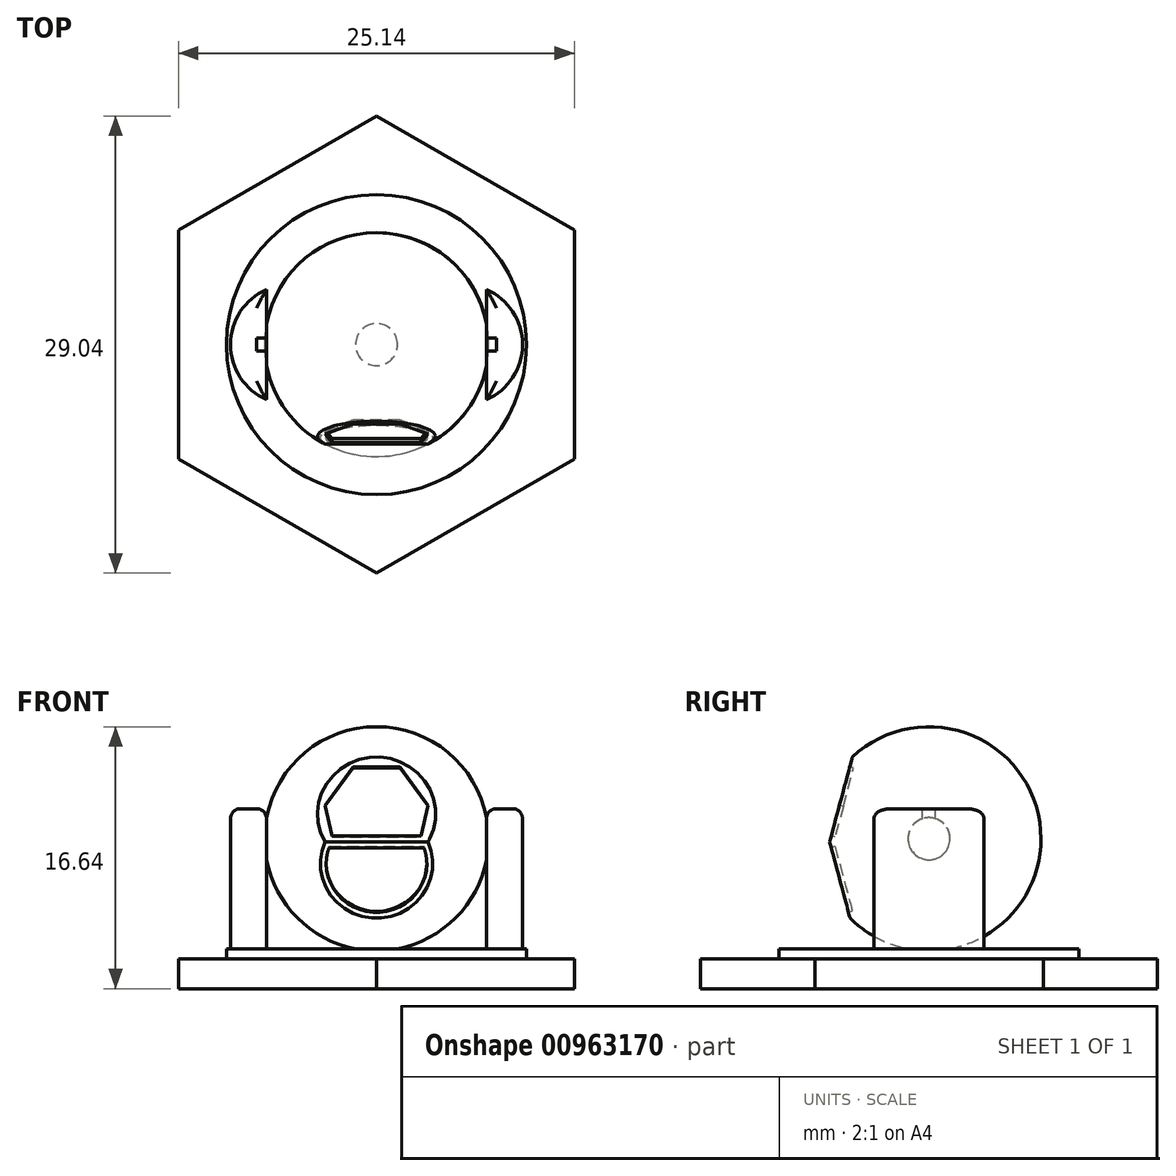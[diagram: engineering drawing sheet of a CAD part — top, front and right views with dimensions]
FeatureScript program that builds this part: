
annotation { "Feature Type Name" : "Feature", "Feature Type Description" : "" }
export const myFeature = defineFeature(function(context is Context, id is Id, definition is map)
    precondition{}
    {
        {
            var Q0;
            Q0=qCreatedBy(makeId("Top.planeOp"),FACE);
            var sketch = newSketch(context, id + "F0", { "sketchPlane" : qUnion([Q0])});
            skCircle(sketch, "E0.cCircle", {"center": v(0, 0) * mm, "radius": 12.57 * mm, "construction": true});
            skLineSegment(sketch, "E0.0", {"start": v(0, 14.52) * mm, "end": v(12.57, 7.26) * mm});
            skLineSegment(sketch, "E0.1", {"start": v(12.57, 7.26) * mm, "end": v(12.57, -7.26) * mm});
            skLineSegment(sketch, "E0.2", {"start": v(12.57, -7.26) * mm, "end": v(0, -14.52) * mm});
            skLineSegment(sketch, "E0.3", {"start": v(0, -14.52) * mm, "end": v(-12.57, -7.26) * mm});
            skLineSegment(sketch, "E0.4", {"start": v(-12.57, -7.26) * mm, "end": v(-12.57, 7.26) * mm});
            skLineSegment(sketch, "E0.5", {"start": v(-12.57, 7.26) * mm, "end": v(0, 14.52) * mm});
            skPoint(sketch, "E0.0.midPoint", {"position": v(6.29, 10.89) * mm});
            skLineSegment(sketch, "E1", {"start": v(-6.99, 3.5) * mm, "end": v(-6.99, -3.5) * mm});
            skArc(sketch, "E2", {"start": v(-6.99, 3.5) * mm, "mid": v(-9.27, 0) * mm, "end": v(-6.99, -3.5) * mm});
            skLineSegment(sketch, "E3.MirrorCS", {"start": v(6.99, 3.5) * mm, "end": v(6.99, -3.5) * mm});
            skArc(sketch, "E4.MirrorCS", {"start": v(6.99, 3.5) * mm, "mid": v(9.27, 0) * mm, "end": v(6.99, -3.5) * mm});
            skCircle(sketch, "E5", {"center": v(0, 0) * mm, "radius": 9.53 * mm});
            skSolve(sketch);
        }
        {
            var Q0;
            Q0=makeQuery(id+"F0.imprint","IMPRINT",FACE,{"disambiguationData":[TD([[makeQuery(id+"F0.imprint","IMPRINT",EDGE,{"derivedFrom":sQuery(id+"F0.wireOp",EDGE,"E0.0")}),-1.0]])]});
            var Q1;
            Q1=makeQuery(id+"F0.imprint","IMPRINT",FACE,{"disambiguationData":[TD([[makeQuery(id+"F0.imprint","IMPRINT",EDGE,{"derivedFrom":sQuery(id+"F0.wireOp",EDGE,"E1")}),1.0]])]});
            extrude(context, id + "F1", {"entities" : qUnion([Q0, Q1]), "depth" : 1.9 * mm, "offsetDistance" : 25.4 * mm});
        }
        {
            var Q0;
            Q0=makeQuery(id+"F0.imprint","IMPRINT",FACE,{"disambiguationData":[TD([[makeQuery(id+"F0.imprint","IMPRINT",EDGE,{"derivedFrom":sQuery(id+"F0.wireOp",EDGE,"E1")}),-1.0]])]});
            var Q1;
            Q1=makeQuery(id+"F0.imprint","IMPRINT",FACE,{"disambiguationData":[TD([[makeQuery(id+"F0.imprint","IMPRINT",EDGE,{"derivedFrom":sQuery(id+"F0.wireOp",EDGE,"E3.MirrorCS")}),1.0]])]});
            extrude(context, id + "F2", {"entities" : qUnion([Q0, Q1]), "operationType" : NewBodyOperationType.ADD, "depth" : 11.43 * mm, "offsetDistance" : 25.4 * mm});
        }
        {
            var Q0;
            Q0=makeQuery(id+"F1.opExtrude","CAP_FACE",FACE,{"disambiguationData":[OSD([sQuery(id+"F0.wireOp",EDGE,"E0.0"),sQuery(id+"F0.wireOp",EDGE,"E0.1"),sQuery(id+"F0.wireOp",EDGE,"E0.2"),sQuery(id+"F0.wireOp",EDGE,"E0.3"),sQuery(id+"F0.wireOp",EDGE,"E0.4"),sQuery(id+"F0.wireOp",EDGE,"E0.5"),sQuery(id+"F0.wireOp",EDGE,"E1"),sQuery(id+"F0.wireOp",EDGE,"E2"),sQuery(id+"F0.wireOp",EDGE,"E3.MirrorCS"),sQuery(id+"F0.wireOp",EDGE,"E4.MirrorCS")])],"isStart":false});
            cPlane(context, id + "F3", {"entities" : qUnion([Q0]), "cplaneType" : CPlaneType.OFFSET, "offset" : 7.62 * mm, "width" : 152.4 * mm, "height" : 152.4 * mm});
        }
        {
            var Q0;
            Q0=qCreatedBy(id+"F3.planeOp",FACE);
            var sketch = newSketch(context, id + "F4", { "sketchPlane" : qUnion([Q0])});
            skLineSegment(sketch, "E6", {"start": v(0, -7.11) * mm, "end": v(0, 7.11) * mm});
            skArc(sketch, "E7", {"start": v(0, 7.11) * mm, "mid": v(-7.11, 0) * mm, "end": v(0, -7.11) * mm});
            skLineSegment(sketch, "E8", {"start": v(-7.11, 0) * mm, "end": v(0, 0) * mm, "construction": true});
            skSolve(sketch);
        }
        {
            var Q0;
            Q0=makeQuery(id+"F4.imprint","IMPRINT",FACE,{"disambiguationData":[TD([[makeQuery(id+"F4.imprint","IMPRINT",EDGE,{"derivedFrom":sQuery(id+"F4.wireOp",EDGE,"E6")}),1.0]])]});
            var Q1;
            Q1=sQuery(id+"F4.wireOp",EDGE,"E6");
            revolve(context, id + "F5", {"operationType" : NewBodyOperationType.ADD, "surfaceOperationType" : NewSurfaceOperationType.NEW, "entities" : qUnion([Q0]), "axis" : qUnion([Q1]), "revolveType" : RevolveType.FULL});
        }
        {
            var Q0;
            Q0=makeQuery(id+"F2.opExtrude","CAP_FACE",FACE,{"disambiguationData":[OSD([sQuery(id+"F0.wireOp",EDGE,"E1"),sQuery(id+"F0.wireOp",EDGE,"E2")])],"isStart":false});
            var Q1;
            Q1=makeQuery(id+"F2.opExtrude","CAP_FACE",FACE,{"disambiguationData":[OSD([sQuery(id+"F0.wireOp",EDGE,"E3.MirrorCS"),sQuery(id+"F0.wireOp",EDGE,"E4.MirrorCS")])],"isStart":false});
            fillet(context, id + "F6", {"entities" : qUnion([Q0, Q1]), "radius" : 0.64 * mm, "tangentPropagation" : true, "allowEdgeOverflow" : false});
        }
        {
            var Q0;
            Q0=makeQuery(id+"F0.imprint","IMPRINT",FACE,{"disambiguationData":[TD([[makeQuery(id+"F0.imprint","IMPRINT",EDGE,{"derivedFrom":sQuery(id+"F0.wireOp",EDGE,"E1")}),1.0]])]});
            extrude(context, id + "F7", {"entities" : qUnion([Q0]), "operationType" : NewBodyOperationType.ADD, "depth" : 2.54 * mm, "offsetDistance" : 25.4 * mm});
        }
        {
            var Q0;
            Q0=sQuery(id+"F4.wireOp",EDGE,"E8");
            cPlane(context, id + "F8", {"entities" : qUnion([Q0]), "cplaneType" : CPlaneType.LINE_ANGLE, "offset" : 25.4 * mm, "angle" : 105 * degree, "width" : 152.4 * mm, "height" : 152.4 * mm});
        }
        {
            var Q0;
            Q0=sQuery(id+"F4.wireOp",EDGE,"E8");
            cPlane(context, id + "F9", {"entities" : qUnion([Q0]), "cplaneType" : CPlaneType.LINE_ANGLE, "offset" : 25.4 * mm, "angle" : 105 * degree, "oppositeDirection" : true, "width" : 152.4 * mm, "height" : 152.4 * mm});
        }
        {
            var Q0;
            Q0=qCreatedBy(id+"F8.planeOp",FACE);
            var sketch = newSketch(context, id + "F10", { "sketchPlane" : qUnion([Q0])});
            skLineSegment(sketch, "E9.bottom", {"start": v(-5.08, -3.68) * mm, "end": v(5.08, -3.68) * mm});
            skLineSegment(sketch, "E9.top", {"start": v(-5.08, -4.95) * mm, "end": v(5.08, -4.95) * mm});
            skLineSegment(sketch, "E9.left", {"start": v(-5.08, -3.68) * mm, "end": v(-5.08, -4.95) * mm});
            skLineSegment(sketch, "E9.right", {"start": v(5.08, -3.68) * mm, "end": v(5.08, -4.95) * mm});
            skSolve(sketch);
        }
        {
            var Q0;
            Q0=makeQuery(id+"F10.imprint","IMPRINT",FACE,{"disambiguationData":[TD([[makeQuery(id+"F10.imprint","IMPRINT",EDGE,{"derivedFrom":sQuery(id+"F10.wireOp",EDGE,"E9.bottom")}),-1.0]])]});
            extrude(context, id + "F11", {"entities" : qUnion([Q0]), "operationType" : NewBodyOperationType.REMOVE, "oppositeDirection" : true, "depth" : 7.62 * mm, "offsetDistance" : 25.4 * mm, "symmetric" : true});
        }
        {
            var Q0;
            Q0=qCreatedBy(id+"F9.planeOp",FACE);
            var sketch = newSketch(context, id + "F12", { "sketchPlane" : qUnion([Q0])});
            skLineSegment(sketch, "E10.bottom", {"start": v(-5.08, 8.5) * mm, "end": v(5.08, 8.5) * mm});
            skLineSegment(sketch, "E10.top", {"start": v(-5.08, 10.41) * mm, "end": v(5.08, 10.41) * mm});
            skLineSegment(sketch, "E10.left", {"start": v(-5.08, 8.5) * mm, "end": v(-5.08, 10.41) * mm});
            skLineSegment(sketch, "E10.right", {"start": v(5.08, 8.5) * mm, "end": v(5.08, 10.41) * mm});
            skSolve(sketch);
        }
        {
            var Q0;
            Q0=makeQuery(id+"F12.imprint","IMPRINT",FACE,{"disambiguationData":[TD([[makeQuery(id+"F12.imprint","IMPRINT",EDGE,{"derivedFrom":sQuery(id+"F12.wireOp",EDGE,"E10.bottom")}),1.0]])]});
            extrude(context, id + "F13", {"entities" : qUnion([Q0]), "operationType" : NewBodyOperationType.REMOVE, "oppositeDirection" : true, "depth" : 7.62 * mm, "offsetDistance" : 25.4 * mm, "symmetric" : true});
        }
        {
            var Q0;
            Q0=makeQuery(id+"F11.boolean.opBoolean","COPY",FACE,{"derivedFrom":makeQuery(id+"F11.opExtrude","SWEPT_FACE",FACE,{"disambiguationData":[OSD([sQuery(id+"F10.wireOp",EDGE,"E9.bottom")])]})});
            var sketch = newSketch(context, id + "F14", { "sketchPlane" : qUnion([Q0])});
            skLineSegment(sketch, "E11.0", {"start": v(-3.01, 10.26) * mm, "end": v(3.01, 10.26) * mm});
            skArc(sketch, "E11.1", {"start": v(-3.01, 10.26) * mm, "mid": v(0, 6) * mm, "end": v(3.01, 10.26) * mm});
            skSolve(sketch);
        }
        {
            var Q0;
            Q0 = qSketchRegion(id + "F14", true);
            extrude(context, id + "F15", {"entities" : qUnion([Q0]), "operationType" : NewBodyOperationType.REMOVE, "oppositeDirection" : true, "depth" : 0.25 * mm, "offsetDistance" : 25.4 * mm});
        }
        {
            var Q0;
            Q0=makeQuery(id+"F13.boolean.opBoolean","COPY",FACE,{"derivedFrom":makeQuery(id+"F13.opExtrude","SWEPT_FACE",FACE,{"disambiguationData":[OSD([sQuery(id+"F12.wireOp",EDGE,"E10.bottom")])]})});
            var sketch = newSketch(context, id + "F16", { "sketchPlane" : qUnion([Q0])});
            skLineSegment(sketch, "E12", {"start": v(-2.82, 7.75) * mm, "end": v(2.82, 7.75) * mm});
            skLineSegment(sketch, "E13", {"start": v(2.82, 7.75) * mm, "end": v(3.27, 9.79) * mm});
            skLineSegment(sketch, "E14", {"start": v(3.27, 9.79) * mm, "end": v(1.48, 12.31) * mm});
            skLineSegment(sketch, "E15", {"start": v(1.48, 12.31) * mm, "end": v(-1.48, 12.31) * mm});
            skLineSegment(sketch, "E16", {"start": v(-1.48, 12.31) * mm, "end": v(-3.27, 9.79) * mm});
            skLineSegment(sketch, "E17", {"start": v(-3.27, 9.79) * mm, "end": v(-2.82, 7.75) * mm});
            skSolve(sketch);
        }
        {
            var Q0;
            Q0=makeQuery(id+"F16.imprint","IMPRINT",FACE,{"disambiguationData":[TD([[makeQuery(id+"F16.imprint","IMPRINT",EDGE,{"derivedFrom":sQuery(id+"F16.wireOp",EDGE,"E12")}),1.0]])]});
            extrude(context, id + "F17", {"entities" : qUnion([Q0]), "operationType" : NewBodyOperationType.REMOVE, "oppositeDirection" : true, "depth" : 0.25 * mm, "offsetDistance" : 25.4 * mm});
        }
    });
